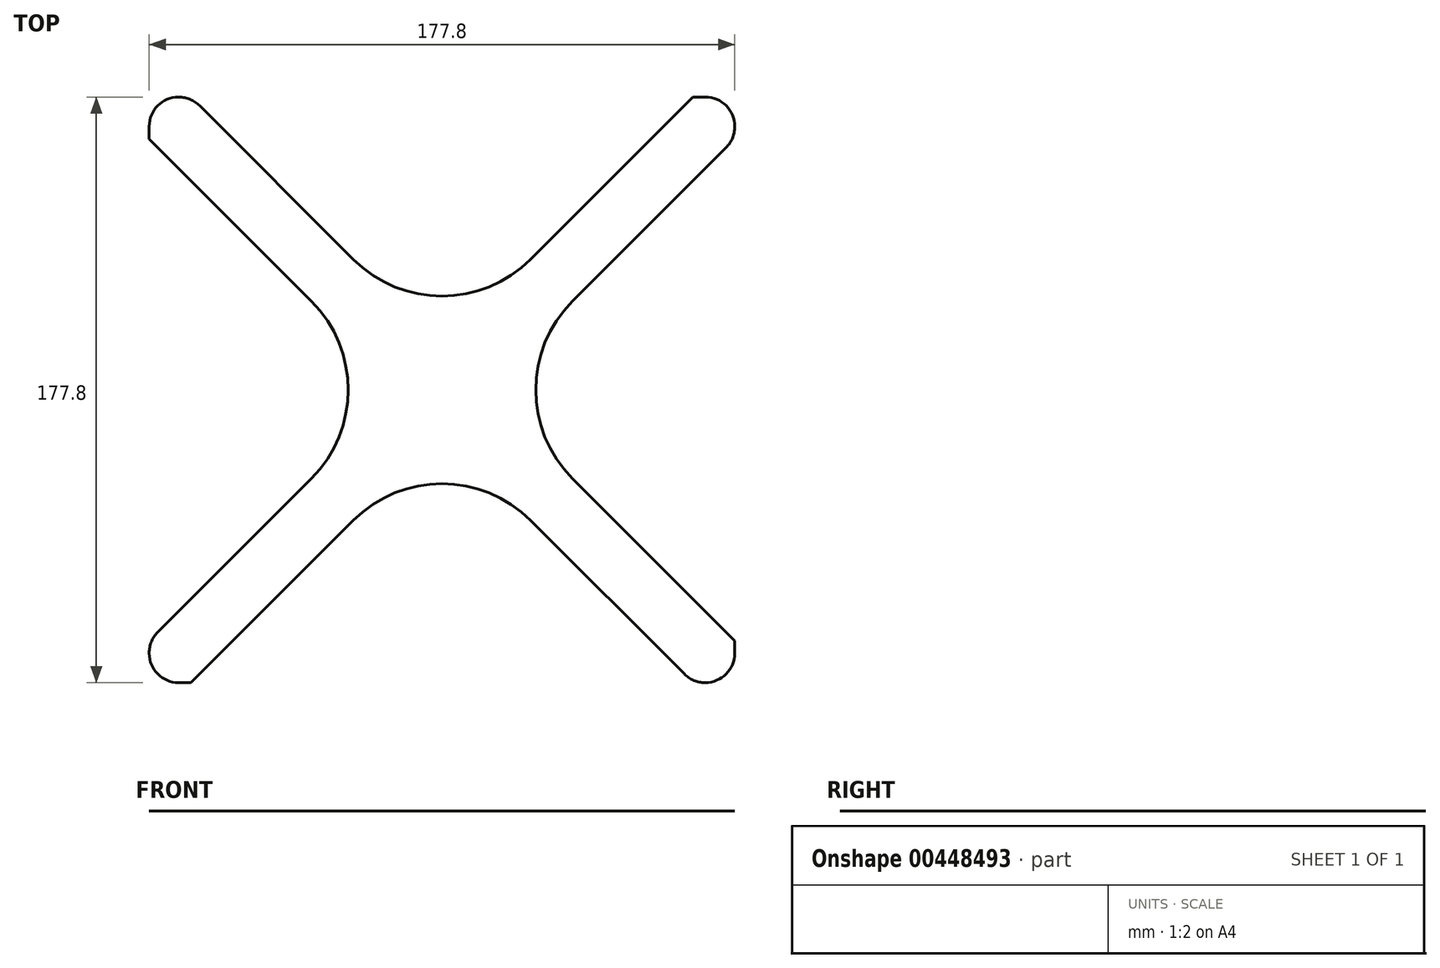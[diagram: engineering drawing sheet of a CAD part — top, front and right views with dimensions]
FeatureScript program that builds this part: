
annotation { "Feature Type Name" : "Feature", "Feature Type Description" : "" }
export const myFeature = defineFeature(function(context is Context, id is Id, definition is map)
    precondition{}
    {
        {
            var Q0;
            Q0=qCreatedBy(makeId("Top.planeOp"),FACE);
            var sketch = newSketch(context, id + "F0", { "sketchPlane" : qUnion([Q0])});
            skLineSegment(sketch, "E0.bottom", {"start": v(88.9, 88.9) * mm, "end": v(-88.9, 88.9) * mm});
            skLineSegment(sketch, "E0.top", {"start": v(88.9, -88.9) * mm, "end": v(-88.9, -88.9) * mm});
            skLineSegment(sketch, "E0.left", {"start": v(88.9, 88.9) * mm, "end": v(88.9, -88.9) * mm});
            skLineSegment(sketch, "E0.right", {"start": v(-88.9, 88.9) * mm, "end": v(-88.9, -88.9) * mm});
            skPoint(sketch, "E0.middle", {"position": v(0, 0) * mm});
            skSolve(sketch);
        }
        {
            var Q0;
            Q0=qSketchRegion(id+"F0",true);
            extrude(context, id + "F1", {"entities" : qUnion([Q0]), "depth" : 1 / 203.2 * mm});
        }
        {
            var Q0;
            Q0=makeQuery(id+"F1.opExtrude","CAP_FACE",FACE,{"disambiguationData":[OSD([sQuery(id+"F0.wireOp",EDGE,"E0.bottom"),sQuery(id+"F0.wireOp",EDGE,"E0.top"),sQuery(id+"F0.wireOp",EDGE,"E0.left"),sQuery(id+"F0.wireOp",EDGE,"E0.right")])],"isStart":false});
            var sketch = newSketch(context, id + "F2", { "sketchPlane" : qUnion([Q0])});
            skLineSegment(sketch, "E1", {"start": v(0, 0) * mm, "end": v(-88.9, 88.9) * mm});
            skLineSegment(sketch, "E2", {"start": v(0, 0) * mm, "end": v(88.9, 88.9) * mm});
            skLineSegment(sketch, "E3", {"start": v(0, 0) * mm, "end": v(88.9, -88.9) * mm});
            skLineSegment(sketch, "E4", {"start": v(0, 0) * mm, "end": v(-88.9, -88.9) * mm});
            skLineSegment(sketch, "E5", {"start": v(0, 12.7) * mm, "end": v(-76.2, 88.9) * mm});
            skLineSegment(sketch, "E6.MirrorCS", {"start": v(-12.7, 0) * mm, "end": v(-88.9, 76.2) * mm});
            skLineSegment(sketch, "E7.MirrorCS", {"start": v(0, 12.7) * mm, "end": v(76.2, 88.9) * mm});
            skLineSegment(sketch, "E8.MirrorCS", {"start": v(12.7, 0) * mm, "end": v(88.9, 76.2) * mm});
            skLineSegment(sketch, "E9.MirrorCS", {"start": v(12.7, 0) * mm, "end": v(88.9, -76.2) * mm});
            skLineSegment(sketch, "E10.MirrorCS", {"start": v(0, -12.7) * mm, "end": v(76.2, -88.9) * mm});
            skLineSegment(sketch, "E11.MirrorCS", {"start": v(0, -12.7) * mm, "end": v(-76.2, -88.9) * mm});
            skLineSegment(sketch, "E12.MirrorCS", {"start": v(-12.7, 0) * mm, "end": v(-88.9, -76.2) * mm});
            skLineSegment(sketch, "E13", {"start": v(-76.2, 88.9) * mm, "end": v(76.2, 88.9) * mm});
            skLineSegment(sketch, "E14", {"start": v(88.9, 76.2) * mm, "end": v(88.9, -76.2) * mm});
            skLineSegment(sketch, "E15", {"start": v(76.2, -88.9) * mm, "end": v(-76.2, -88.9) * mm});
            skLineSegment(sketch, "E16", {"start": v(-88.9, -76.2) * mm, "end": v(-88.9, 76.2) * mm});
            skSolve(sketch);
        }
        {
            var Q0;
            Q0=makeQuery(id+"F2.imprint","IMPRINT",FACE,{"disambiguationData":[TD([[makeQuery(id+"F2.imprint","IMPRINT",EDGE,{"derivedFrom":sQuery(id+"F2.wireOp",EDGE,"E5")}),-1.0]])]});
            var Q1;
            Q1=makeQuery(id+"F2.imprint","IMPRINT",FACE,{"disambiguationData":[TD([[makeQuery(id+"F2.imprint","IMPRINT",EDGE,{"derivedFrom":sQuery(id+"F2.wireOp",EDGE,"E8.MirrorCS")}),-1.0]])]});
            var Q2;
            Q2=makeQuery(id+"F2.imprint","IMPRINT",FACE,{"disambiguationData":[TD([[makeQuery(id+"F2.imprint","IMPRINT",EDGE,{"derivedFrom":sQuery(id+"F2.wireOp",EDGE,"E10.MirrorCS")}),-1.0]])]});
            var Q3;
            Q3=makeQuery(id+"F2.imprint","IMPRINT",FACE,{"disambiguationData":[TD([[makeQuery(id+"F2.imprint","IMPRINT",EDGE,{"derivedFrom":sQuery(id+"F2.wireOp",EDGE,"E6.MirrorCS")}),1.0]])]});
            extrude(context, id + "F3", {"entities" : qUnion([Q0, Q1, Q2, Q3]), "operationType" : NewBodyOperationType.REMOVE, "endBound" : BoundingType.THROUGH_ALL, "oppositeDirection" : true, "depth" : 25.4 * mm});
        }
        {
            var Q0;
            Q0=makeQuery(id+"F3.boolean.opBoolean","COPY",EDGE,{"derivedFrom":makeQuery(id+"F3.opExtrude","SWEPT_EDGE",EDGE,{"disambiguationData":[OSD([sQuery(id+"F2.wireOp",EDGE,"E10.MirrorCS"),sQuery(id+"F2.wireOp",EDGE,"E11.MirrorCS")])]})});
            var Q1;
            Q1=makeQuery(id+"F3.boolean.opBoolean","COPY",EDGE,{"derivedFrom":makeQuery(id+"F3.opExtrude","SWEPT_EDGE",EDGE,{"disambiguationData":[OSD([sQuery(id+"F2.wireOp",EDGE,"E8.MirrorCS"),sQuery(id+"F2.wireOp",EDGE,"E9.MirrorCS")])]})});
            var Q2;
            Q2=makeQuery(id+"F3.boolean.opBoolean","COPY",EDGE,{"derivedFrom":makeQuery(id+"F3.opExtrude","SWEPT_EDGE",EDGE,{"disambiguationData":[OSD([sQuery(id+"F2.wireOp",EDGE,"E5"),sQuery(id+"F2.wireOp",EDGE,"E7.MirrorCS")])]})});
            var Q3;
            Q3=makeQuery(id+"F3.boolean.opBoolean","COPY",EDGE,{"derivedFrom":makeQuery(id+"F3.opExtrude","SWEPT_EDGE",EDGE,{"disambiguationData":[OSD([sQuery(id+"F2.wireOp",EDGE,"E6.MirrorCS"),sQuery(id+"F2.wireOp",EDGE,"E12.MirrorCS")])]})});
            fillet(context, id + "F4", {"entities" : qUnion([Q0, Q1, Q2, Q3]), "radius" : 38.1 * mm, "tangentPropagation" : true, "allowEdgeOverflow" : false});
        }
        {
            var Q0;
            Q0=makeQuery(id+"F1.opExtrude","SWEPT_EDGE",EDGE,{"disambiguationData":[OSD([sQuery(id+"F0.wireOp",EDGE,"E0.bottom"),sQuery(id+"F0.wireOp",EDGE,"E0.left")])]});
            var Q1;
            Q1=makeQuery(id+"F3.boolean.opBoolean","COPY",EDGE,{"derivedFrom":makeQuery(id+"F3.opExtrude","SWEPT_EDGE",EDGE,{"disambiguationData":[OSD([sQuery(id+"F0.wireOp",EDGE,"E0.left"),sQuery(id+"F2.wireOp",EDGE,"E8.MirrorCS"),sQuery(id+"F2.wireOp",EDGE,"E14")])]})});
            var Q2;
            Q2=makeQuery(id+"F3.boolean.opBoolean","COPY",EDGE,{"derivedFrom":makeQuery(id+"F3.opExtrude","SWEPT_EDGE",EDGE,{"disambiguationData":[OSD([sQuery(id+"F0.wireOp",EDGE,"E0.left"),sQuery(id+"F2.wireOp",EDGE,"E9.MirrorCS"),sQuery(id+"F2.wireOp",EDGE,"E14")])]})});
            var Q3;
            Q3=makeQuery(id+"F1.opExtrude","SWEPT_EDGE",EDGE,{"disambiguationData":[OSD([sQuery(id+"F0.wireOp",EDGE,"E0.top"),sQuery(id+"F0.wireOp",EDGE,"E0.left")])]});
            var Q4;
            Q4=makeQuery(id+"F3.boolean.opBoolean","COPY",EDGE,{"derivedFrom":makeQuery(id+"F3.opExtrude","SWEPT_EDGE",EDGE,{"disambiguationData":[OSD([sQuery(id+"F0.wireOp",EDGE,"E0.top"),sQuery(id+"F2.wireOp",EDGE,"E10.MirrorCS"),sQuery(id+"F2.wireOp",EDGE,"E15")])]})});
            var Q5;
            Q5=makeQuery(id+"F3.boolean.opBoolean","COPY",EDGE,{"derivedFrom":makeQuery(id+"F3.opExtrude","SWEPT_EDGE",EDGE,{"disambiguationData":[OSD([sQuery(id+"F0.wireOp",EDGE,"E0.top"),sQuery(id+"F2.wireOp",EDGE,"E11.MirrorCS"),sQuery(id+"F2.wireOp",EDGE,"E15")])]})});
            var Q6;
            Q6=makeQuery(id+"F1.opExtrude","SWEPT_EDGE",EDGE,{"disambiguationData":[OSD([sQuery(id+"F0.wireOp",EDGE,"E0.top"),sQuery(id+"F0.wireOp",EDGE,"E0.right")])]});
            var Q7;
            Q7=makeQuery(id+"F3.boolean.opBoolean","COPY",EDGE,{"derivedFrom":makeQuery(id+"F3.opExtrude","SWEPT_EDGE",EDGE,{"disambiguationData":[OSD([sQuery(id+"F0.wireOp",EDGE,"E0.right"),sQuery(id+"F2.wireOp",EDGE,"E12.MirrorCS"),sQuery(id+"F2.wireOp",EDGE,"E16")])]})});
            var Q8;
            Q8=makeQuery(id+"F3.boolean.opBoolean","COPY",EDGE,{"derivedFrom":makeQuery(id+"F3.opExtrude","SWEPT_EDGE",EDGE,{"disambiguationData":[OSD([sQuery(id+"F0.wireOp",EDGE,"E0.right"),sQuery(id+"F2.wireOp",EDGE,"E6.MirrorCS"),sQuery(id+"F2.wireOp",EDGE,"E16")])]})});
            var Q9;
            Q9=makeQuery(id+"F1.opExtrude","SWEPT_EDGE",EDGE,{"disambiguationData":[OSD([sQuery(id+"F0.wireOp",EDGE,"E0.bottom"),sQuery(id+"F0.wireOp",EDGE,"E0.right")])]});
            var Q10;
            Q10=makeQuery(id+"F3.boolean.opBoolean","COPY",EDGE,{"derivedFrom":makeQuery(id+"F3.opExtrude","SWEPT_EDGE",EDGE,{"disambiguationData":[OSD([sQuery(id+"F0.wireOp",EDGE,"E0.bottom"),sQuery(id+"F2.wireOp",EDGE,"E5"),sQuery(id+"F2.wireOp",EDGE,"E13")])]})});
            var Q11;
            Q11=makeQuery(id+"F3.boolean.opBoolean","COPY",EDGE,{"derivedFrom":makeQuery(id+"F3.opExtrude","SWEPT_EDGE",EDGE,{"disambiguationData":[OSD([sQuery(id+"F0.wireOp",EDGE,"E0.bottom"),sQuery(id+"F2.wireOp",EDGE,"E7.MirrorCS"),sQuery(id+"F2.wireOp",EDGE,"E13")])]})});
            fillet(context, id + "F5", {"entities" : qUnion([Q0, Q1, Q2, Q3, Q4, Q5, Q6, Q7, Q8, Q9, Q10, Q11]), "radius" : 8.9 * mm, "tangentPropagation" : true, "allowEdgeOverflow" : false});
        }
    });
